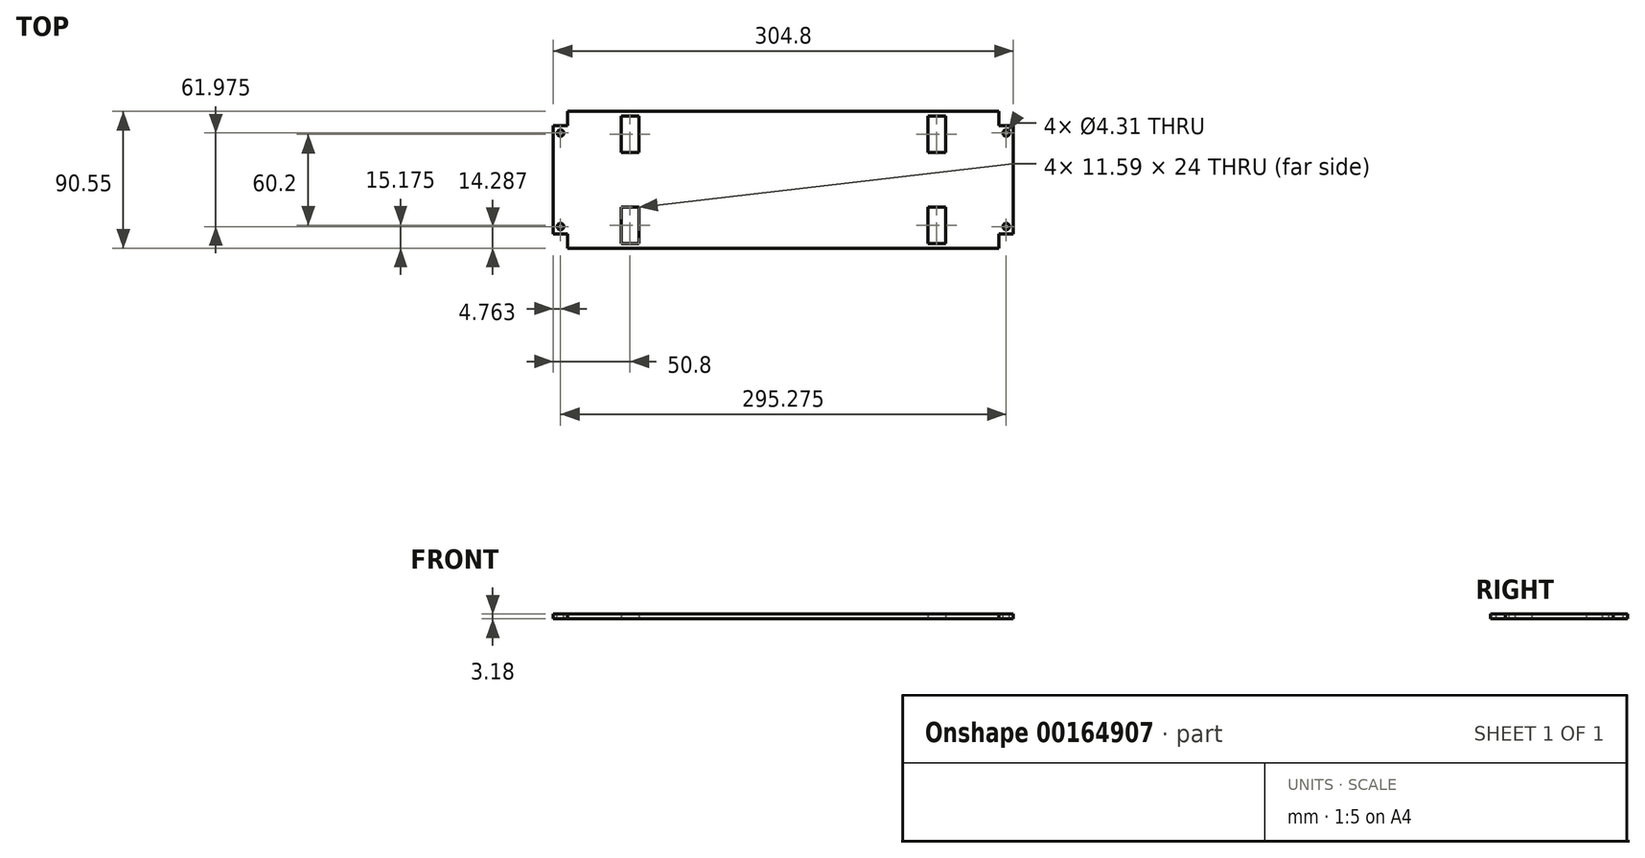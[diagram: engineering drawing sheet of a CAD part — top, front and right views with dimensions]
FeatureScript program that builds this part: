
annotation { "Feature Type Name" : "Feature", "Feature Type Description" : "" }
export const myFeature = defineFeature(function(context is Context, id is Id, definition is map)
    precondition{}
    {
        {
            var Q0;
            Q0=qCreatedBy(makeId("Top.planeOp"),FACE);
            var sketch = newSketch(context, id + "F0", { "sketchPlane" : qUnion([Q0])});
            skLineSegment(sketch, "E0.bottom", {"start": v(0, 0) * mm, "end": v(304.8, 0) * mm});
            skLineSegment(sketch, "E0.top", {"start": v(0, -90.55) * mm, "end": v(304.8, -90.55) * mm});
            skLineSegment(sketch, "E0.left", {"start": v(0, 0) * mm, "end": v(0, -90.55) * mm});
            skLineSegment(sketch, "E0.right", {"start": v(304.8, 0) * mm, "end": v(304.8, -90.55) * mm});
            skLineSegment(sketch, "E1", {"start": v(152.4, 0) * mm, "end": v(152.4, -90.55) * mm, "construction": true});
            skLineSegment(sketch, "E2.bottom", {"start": v(254, -15.18) * mm, "end": v(50.8, -15.18) * mm, "construction": true});
            skLineSegment(sketch, "E2.top", {"start": v(254, -75.38) * mm, "end": v(50.8, -75.38) * mm, "construction": true});
            skLineSegment(sketch, "E2.left", {"start": v(254, -15.18) * mm, "end": v(254, -75.38) * mm, "construction": true});
            skLineSegment(sketch, "E2.right", {"start": v(50.8, -15.18) * mm, "end": v(50.8, -75.38) * mm, "construction": true});
            skPoint(sketch, "E2.middle", {"position": v(152.4, -45.28) * mm});
            skLineSegment(sketch, "E3.bottom", {"start": v(259.8, -3.18) * mm, "end": v(248.2, -3.18) * mm});
            skLineSegment(sketch, "E3.top", {"start": v(259.8, -27.17) * mm, "end": v(248.2, -27.17) * mm});
            skLineSegment(sketch, "E3.left", {"start": v(259.8, -3.18) * mm, "end": v(259.8, -27.18) * mm});
            skLineSegment(sketch, "E3.right", {"start": v(248.2, -3.18) * mm, "end": v(248.2, -27.18) * mm});
            skPoint(sketch, "E3.middle", {"position": v(254, -15.17) * mm});
            skLineSegment(sketch, "E4.bottom", {"start": v(259.8, -87.38) * mm, "end": v(248.2, -87.38) * mm});
            skLineSegment(sketch, "E4.top", {"start": v(259.8, -63.38) * mm, "end": v(248.2, -63.38) * mm});
            skLineSegment(sketch, "E4.left", {"start": v(259.8, -87.38) * mm, "end": v(259.8, -63.38) * mm});
            skLineSegment(sketch, "E4.right", {"start": v(248.2, -87.38) * mm, "end": v(248.2, -63.38) * mm});
            skPoint(sketch, "E4.middle", {"position": v(254, -75.38) * mm});
            skLineSegment(sketch, "E5.bottom", {"start": v(45, -87.38) * mm, "end": v(56.6, -87.38) * mm});
            skLineSegment(sketch, "E5.top", {"start": v(45, -63.38) * mm, "end": v(56.6, -63.38) * mm});
            skLineSegment(sketch, "E5.left", {"start": v(45, -87.38) * mm, "end": v(45, -63.38) * mm});
            skLineSegment(sketch, "E5.right", {"start": v(56.6, -87.38) * mm, "end": v(56.6, -63.38) * mm});
            skPoint(sketch, "E5.middle", {"position": v(50.8, -75.38) * mm});
            skLineSegment(sketch, "E6.bottom", {"start": v(45, -27.18) * mm, "end": v(56.6, -27.18) * mm});
            skLineSegment(sketch, "E6.top", {"start": v(45, -3.17) * mm, "end": v(56.6, -3.17) * mm});
            skLineSegment(sketch, "E6.left", {"start": v(45, -27.18) * mm, "end": v(45, -3.18) * mm});
            skLineSegment(sketch, "E6.right", {"start": v(56.6, -27.17) * mm, "end": v(56.6, -3.18) * mm});
            skPoint(sketch, "E6.middle", {"position": v(50.8, -15.17) * mm});
            skSolve(sketch);
        }
        {
            var Q0;
            Q0=qSketchRegion(id+"F0",true);
            extrude(context, id + "F1", {"entities" : qUnion([Q0]), "depth" : 3.17 * mm});
        }
        {
            var Q0;
            Q0=makeQuery(id+"F1.opExtrude","CAP_FACE",FACE,{"disambiguationData":[OSD([sQuery(id+"F0.wireOp",EDGE,"E0.bottom"),sQuery(id+"F0.wireOp",EDGE,"E0.top"),sQuery(id+"F0.wireOp",EDGE,"E0.left"),sQuery(id+"F0.wireOp",EDGE,"E0.right"),sQuery(id+"F0.wireOp",EDGE,"E3.bottom"),sQuery(id+"F0.wireOp",EDGE,"E3.top"),sQuery(id+"F0.wireOp",EDGE,"E3.left"),sQuery(id+"F0.wireOp",EDGE,"E3.right"),sQuery(id+"F0.wireOp",EDGE,"E4.bottom"),sQuery(id+"F0.wireOp",EDGE,"E4.top"),sQuery(id+"F0.wireOp",EDGE,"E4.left"),sQuery(id+"F0.wireOp",EDGE,"E4.right"),sQuery(id+"F0.wireOp",EDGE,"E5.bottom"),sQuery(id+"F0.wireOp",EDGE,"E5.top"),sQuery(id+"F0.wireOp",EDGE,"E5.left"),sQuery(id+"F0.wireOp",EDGE,"E5.right"),sQuery(id+"F0.wireOp",EDGE,"E6.bottom"),sQuery(id+"F0.wireOp",EDGE,"E6.top"),sQuery(id+"F0.wireOp",EDGE,"E6.left"),sQuery(id+"F0.wireOp",EDGE,"E6.right")])],"isStart":false});
            var sketch = newSketch(context, id + "F2", { "sketchPlane" : qUnion([Q0])});
            skLineSegment(sketch, "E7", {"start": v(152.4, 0) * mm, "end": v(152.4, -90.55) * mm, "construction": true});
            skLineSegment(sketch, "E8.bottom", {"start": v(4.76, -14.29) * mm, "end": v(300.04, -14.29) * mm, "construction": true});
            skLineSegment(sketch, "E8.top", {"start": v(4.76, -76.26) * mm, "end": v(300.04, -76.26) * mm, "construction": true});
            skLineSegment(sketch, "E8.left", {"start": v(4.76, -14.29) * mm, "end": v(4.76, -76.26) * mm, "construction": true});
            skLineSegment(sketch, "E8.right", {"start": v(300.04, -14.29) * mm, "end": v(300.04, -76.26) * mm, "construction": true});
            skPoint(sketch, "E8.middle", {"position": v(152.4, -45.28) * mm});
            skLineSegment(sketch, "E9.bottom", {"start": v(4.76, -76.26) * mm, "end": v(0, -76.26) * mm, "construction": true});
            skLineSegment(sketch, "E9.top", {"start": v(4.76, -90.55) * mm, "end": v(0, -90.55) * mm, "construction": true});
            skLineSegment(sketch, "E9.left", {"start": v(4.76, -76.26) * mm, "end": v(4.76, -90.55) * mm, "construction": true});
            skLineSegment(sketch, "E9.right", {"start": v(0, -76.26) * mm, "end": v(0, -90.55) * mm, "construction": true});
            skCircle(sketch, "E10", {"center": v(4.76, -14.29) * mm, "radius": 2.15 * mm});
            skCircle(sketch, "E11", {"center": v(4.76, -76.26) * mm, "radius": 2.15 * mm});
            skCircle(sketch, "E12", {"center": v(300.04, -76.26) * mm, "radius": 2.15 * mm});
            skCircle(sketch, "E13", {"center": v(300.04, -14.29) * mm, "radius": 2.15 * mm});
            skSolve(sketch);
        }
        {
            var Q0;
            Q0=qSketchRegion(id+"F2",true);
            var Q1;
            Q1=makeQuery(id+"F1.opExtrude","CAP_FACE",FACE,{"disambiguationData":[OSD([sQuery(id+"F0.wireOp",EDGE,"E0.bottom"),sQuery(id+"F0.wireOp",EDGE,"E0.top"),sQuery(id+"F0.wireOp",EDGE,"E0.left"),sQuery(id+"F0.wireOp",EDGE,"E0.right"),sQuery(id+"F0.wireOp",EDGE,"E3.bottom"),sQuery(id+"F0.wireOp",EDGE,"E3.top"),sQuery(id+"F0.wireOp",EDGE,"E3.left"),sQuery(id+"F0.wireOp",EDGE,"E3.right"),sQuery(id+"F0.wireOp",EDGE,"E4.bottom"),sQuery(id+"F0.wireOp",EDGE,"E4.top"),sQuery(id+"F0.wireOp",EDGE,"E4.left"),sQuery(id+"F0.wireOp",EDGE,"E4.right"),sQuery(id+"F0.wireOp",EDGE,"E5.bottom"),sQuery(id+"F0.wireOp",EDGE,"E5.top"),sQuery(id+"F0.wireOp",EDGE,"E5.left"),sQuery(id+"F0.wireOp",EDGE,"E5.right"),sQuery(id+"F0.wireOp",EDGE,"E6.bottom"),sQuery(id+"F0.wireOp",EDGE,"E6.top"),sQuery(id+"F0.wireOp",EDGE,"E6.left"),sQuery(id+"F0.wireOp",EDGE,"E6.right")])],"isStart":true});
            extrude(context, id + "F3", {"entities" : qUnion([Q0]), "operationType" : NewBodyOperationType.REMOVE, "endBound" : BoundingType.UP_TO_SURFACE, "oppositeDirection" : true, "endBoundEntityFace" : qUnion([Q1]), "depth" : 25.4 * mm});
        }
        {
            var Q0;
            Q0=makeQuery(id+"F1.opExtrude","CAP_FACE",FACE,{"disambiguationData":[OSD([sQuery(id+"F0.wireOp",EDGE,"E0.bottom"),sQuery(id+"F0.wireOp",EDGE,"E0.top"),sQuery(id+"F0.wireOp",EDGE,"E0.left"),sQuery(id+"F0.wireOp",EDGE,"E0.right"),sQuery(id+"F0.wireOp",EDGE,"E3.bottom"),sQuery(id+"F0.wireOp",EDGE,"E3.top"),sQuery(id+"F0.wireOp",EDGE,"E3.left"),sQuery(id+"F0.wireOp",EDGE,"E3.right"),sQuery(id+"F0.wireOp",EDGE,"E4.bottom"),sQuery(id+"F0.wireOp",EDGE,"E4.top"),sQuery(id+"F0.wireOp",EDGE,"E4.left"),sQuery(id+"F0.wireOp",EDGE,"E4.right"),sQuery(id+"F0.wireOp",EDGE,"E5.bottom"),sQuery(id+"F0.wireOp",EDGE,"E5.top"),sQuery(id+"F0.wireOp",EDGE,"E5.left"),sQuery(id+"F0.wireOp",EDGE,"E5.right"),sQuery(id+"F0.wireOp",EDGE,"E6.bottom"),sQuery(id+"F0.wireOp",EDGE,"E6.top"),sQuery(id+"F0.wireOp",EDGE,"E6.left"),sQuery(id+"F0.wireOp",EDGE,"E6.right")])],"isStart":false});
            var sketch = newSketch(context, id + "F4", { "sketchPlane" : qUnion([Q0])});
            skLineSegment(sketch, "E14.bottom", {"start": v(304.8, 0) * mm, "end": v(295.28, 0) * mm});
            skLineSegment(sketch, "E14.top", {"start": v(304.8, -9.53) * mm, "end": v(295.28, -9.53) * mm});
            skLineSegment(sketch, "E14.left", {"start": v(304.8, 0) * mm, "end": v(304.8, -9.53) * mm});
            skLineSegment(sketch, "E14.right", {"start": v(295.28, 0) * mm, "end": v(295.28, -9.53) * mm});
            skLineSegment(sketch, "E15.bottom", {"start": v(304.8, -90.55) * mm, "end": v(295.28, -90.55) * mm});
            skLineSegment(sketch, "E15.top", {"start": v(304.8, -81.03) * mm, "end": v(295.28, -81.03) * mm});
            skLineSegment(sketch, "E15.left", {"start": v(304.8, -90.55) * mm, "end": v(304.8, -81.03) * mm});
            skLineSegment(sketch, "E15.right", {"start": v(295.28, -90.55) * mm, "end": v(295.28, -81.03) * mm});
            skLineSegment(sketch, "E16.bottom", {"start": v(0, -90.55) * mm, "end": v(9.53, -90.55) * mm});
            skLineSegment(sketch, "E16.top", {"start": v(0, -81.03) * mm, "end": v(9.53, -81.03) * mm});
            skLineSegment(sketch, "E16.left", {"start": v(0, -90.55) * mm, "end": v(0, -81.03) * mm});
            skLineSegment(sketch, "E16.right", {"start": v(9.53, -90.55) * mm, "end": v(9.53, -81.03) * mm});
            skLineSegment(sketch, "E17.bottom", {"start": v(0, 0) * mm, "end": v(9.53, 0) * mm});
            skLineSegment(sketch, "E17.top", {"start": v(0, -9.53) * mm, "end": v(9.53, -9.53) * mm});
            skLineSegment(sketch, "E17.left", {"start": v(0, 0) * mm, "end": v(0, -9.53) * mm});
            skLineSegment(sketch, "E17.right", {"start": v(9.53, 0) * mm, "end": v(9.53, -9.53) * mm});
            skSolve(sketch);
        }
        {
            var Q0;
            Q0=qSketchRegion(id+"F4",true);
            var Q1;
            Q1=makeQuery(id+"F1.opExtrude","CAP_FACE",FACE,{"disambiguationData":[OSD([sQuery(id+"F0.wireOp",EDGE,"E0.bottom"),sQuery(id+"F0.wireOp",EDGE,"E0.top"),sQuery(id+"F0.wireOp",EDGE,"E0.left"),sQuery(id+"F0.wireOp",EDGE,"E0.right"),sQuery(id+"F0.wireOp",EDGE,"E3.bottom"),sQuery(id+"F0.wireOp",EDGE,"E3.top"),sQuery(id+"F0.wireOp",EDGE,"E3.left"),sQuery(id+"F0.wireOp",EDGE,"E3.right"),sQuery(id+"F0.wireOp",EDGE,"E4.bottom"),sQuery(id+"F0.wireOp",EDGE,"E4.top"),sQuery(id+"F0.wireOp",EDGE,"E4.left"),sQuery(id+"F0.wireOp",EDGE,"E4.right"),sQuery(id+"F0.wireOp",EDGE,"E5.bottom"),sQuery(id+"F0.wireOp",EDGE,"E5.top"),sQuery(id+"F0.wireOp",EDGE,"E5.left"),sQuery(id+"F0.wireOp",EDGE,"E5.right"),sQuery(id+"F0.wireOp",EDGE,"E6.bottom"),sQuery(id+"F0.wireOp",EDGE,"E6.top"),sQuery(id+"F0.wireOp",EDGE,"E6.left"),sQuery(id+"F0.wireOp",EDGE,"E6.right")])],"isStart":true});
            extrude(context, id + "F5", {"entities" : qUnion([Q0]), "operationType" : NewBodyOperationType.REMOVE, "endBound" : BoundingType.UP_TO_SURFACE, "oppositeDirection" : true, "endBoundEntityFace" : qUnion([Q1]), "depth" : 25.4 * mm});
        }
    });
